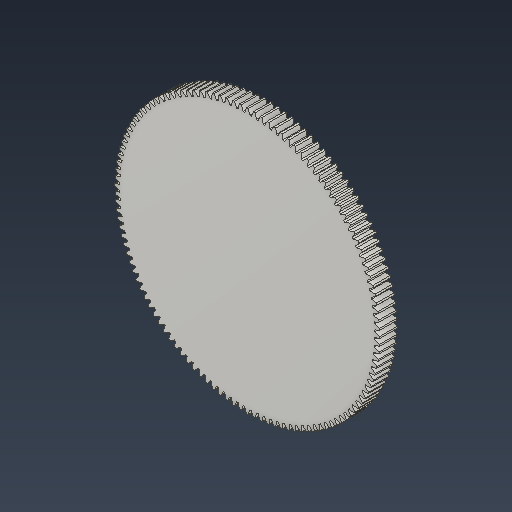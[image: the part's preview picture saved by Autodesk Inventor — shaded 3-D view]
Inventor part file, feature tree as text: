
AUTODESK INVENTOR PART (.ipt)
format: ipt  version: 2022 (Build 260153000, 153)  size: 613,376 bytes
history: native  units: mm (DEFAULTED — no unit token found)
features: plane x3, other x3, sketch x2, extrude x1
ambient origin geometry x8: Origin, YZ Plane, XZ Plane, XY Plane, X Axis, Y Axis, Z Axis, Center Point
bodies: Solid1 (feature_tree)
feature tree (9):
  extrude  "Extrusion1"  Depth=20.0mm TaperAngle=0.0deg
  plane  "Work Plane2"
  plane  "Work Plane8"
  plane  "Work Plane9"
  other  "Spur Gear"
  sketch  "Sketch1"  dims[d0=305.0mm d1=20.0mm d2=0.0mm]
  sketch  "Sketch2"  dims[d3=300.0mm d4=10.0mm d5=0.0mm d16=300.0mm d17=0.0mm d34=0.261799mm d39=0.0mm d41=0.0mm d43=300.0mm d46=300.0mm d47=0.0mm d48=0.0mm]
  other  "Srf1"
  other  "Pitch Diameter"
